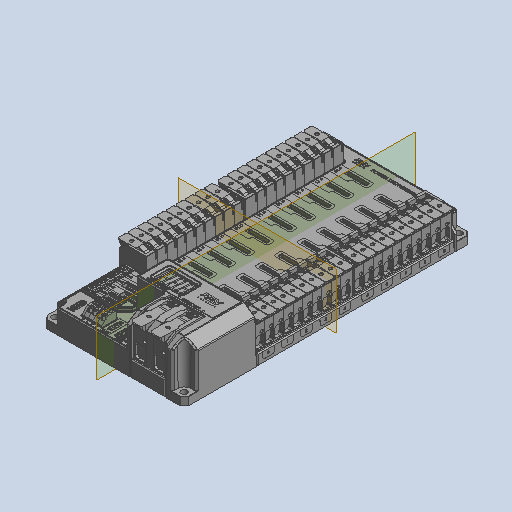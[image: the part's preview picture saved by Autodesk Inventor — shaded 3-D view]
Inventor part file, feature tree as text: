
AUTODESK INVENTOR PART (.ipt)
format: ipt  version: 2023 (Build 270158000, 158)  size: 30,594,048 bytes
history: native  units: mm (DEFAULTED — no unit token found)
features: other x402, plane x2
ambient origin geometry x8: Origin, YZ Plane, XZ Plane, XY Plane, X Axis, Y Axis, Z Axis, Center Point
bodies: Solid1 (feature_tree), Solid2 (feature_tree), Solid3 (feature_tree), Solid4 (feature_tree), Solid5 (feature_tree), Solid6 (feature_tree), Solid7 (feature_tree), Solid8 (feature_tree), Solid9 (feature_tree), Solid10 (feature_tree), Solid11 (feature_tree), Solid12 (feature_tree), Solid13 (feature_tree), Solid14 (feature_tree), Solid15 (feature_tree), Solid16 (feature_tree), Solid17 (feature_tree), Solid18 (feature_tree), Solid19 (feature_tree), Solid20 (feature_tree), Solid21 (feature_tree), Solid22 (feature_tree), Solid23 (feature_tree), Solid24 (feature_tree), Solid25 (feature_tree), Solid26 (feature_tree), Solid27 (feature_tree), Solid28 (feature_tree), Solid29 (feature_tree), Solid30 (feature_tree), Solid31 (feature_tree), Solid32 (feature_tree), Solid33 (feature_tree), Solid34 (feature_tree), Solid35 (feature_tree), Solid36 (feature_tree), Solid37 (feature_tree), Solid38 (feature_tree), Solid39 (feature_tree), Solid40 (feature_tree), Solid41 (feature_tree), Solid42 (feature_tree), Solid43 (feature_tree), Solid44 (feature_tree), Solid45 (feature_tree), Solid46 (feature_tree), Solid47 (feature_tree), Solid48 (feature_tree), Solid49 (feature_tree), Solid50 (feature_tree), Solid51 (feature_tree), Solid52 (feature_tree), Solid53 (feature_tree), Solid54 (feature_tree), Solid55 (feature_tree), Solid56 (feature_tree), Solid57 (feature_tree), Solid58 (feature_tree), Solid59 (feature_tree), Solid60 (feature_tree), Solid61 (feature_tree), Solid62 (feature_tree), Solid63 (feature_tree), Solid64 (feature_tree), Solid65 (feature_tree), Solid66 (feature_tree), Solid67 (feature_tree), Solid68 (feature_tree), Solid69 (feature_tree), Solid70 (feature_tree), Solid71 (feature_tree), Solid72 (feature_tree), Solid73 (feature_tree), Solid74 (feature_tree), Solid75 (feature_tree), Solid76 (feature_tree), Solid77 (feature_tree), Solid78 (feature_tree), Solid79 (feature_tree), Solid80 (feature_tree), Solid81 (feature_tree), Solid82 (feature_tree), Solid83 (feature_tree), Solid84 (feature_tree), Solid85 (feature_tree), Solid86 (feature_tree), Solid87 (feature_tree), Solid88 (feature_tree), Solid89 (feature_tree), Solid90 (feature_tree), Solid91 (feature_tree), Solid92 (feature_tree), Solid93 (feature_tree), Solid94 (feature_tree), Solid95 (feature_tree), Solid96 (feature_tree), Solid97 (feature_tree), Solid98 (feature_tree), Solid99 (feature_tree), Solid100 (feature_tree), Solid101 (feature_tree), Solid102 (feature_tree), Solid103 (feature_tree), Solid104 (feature_tree), Solid105 (feature_tree), Solid106 (feature_tree), Solid107 (feature_tree), Solid108 (feature_tree), Solid109 (feature_tree), Solid110 (feature_tree), Solid111 (feature_tree), Solid112 (feature_tree), Solid113 (feature_tree), Solid114 (feature_tree), Solid115 (feature_tree), Solid116 (feature_tree), Solid117 (feature_tree), Solid118 (feature_tree), Solid119 (feature_tree), Solid120 (feature_tree), Solid121 (feature_tree), Solid122 (feature_tree), Solid123 (feature_tree), Solid124 (feature_tree), Solid125 (feature_tree), Solid126 (feature_tree), Solid127 (feature_tree), Solid128 (feature_tree), Solid129 (feature_tree), Solid130 (feature_tree), Solid131 (feature_tree), Solid132 (feature_tree), Solid133 (feature_tree), Solid134 (feature_tree), Solid135 (feature_tree), Solid136 (feature_tree), Solid137 (feature_tree), Solid138 (feature_tree), Solid139 (feature_tree), Solid140 (feature_tree), Solid141 (feature_tree), Solid142 (feature_tree), Solid143 (feature_tree), Solid144 (feature_tree), Solid145 (feature_tree), Solid146 (feature_tree), Solid147 (feature_tree), Solid148 (feature_tree), Solid149 (feature_tree), Solid150 (feature_tree), Solid151 (feature_tree), Solid152 (feature_tree), Solid153 (feature_tree), Solid154 (feature_tree), Solid155 (feature_tree), Solid156 (feature_tree), Solid157 (feature_tree), Solid158 (feature_tree), Solid159 (feature_tree), Solid160 (feature_tree), Solid161 (feature_tree), Solid162 (feature_tree), Solid163 (feature_tree), Solid164 (feature_tree), Solid165 (feature_tree), Solid166 (feature_tree), Solid167 (feature_tree), Solid168 (feature_tree), Solid169 (feature_tree), Solid170 (feature_tree), Solid171 (feature_tree), Solid172 (feature_tree), Solid173 (feature_tree), Solid174 (feature_tree), Solid175 (feature_tree), Solid176 (feature_tree), Solid177 (feature_tree), Solid178 (feature_tree), Solid179 (feature_tree), Solid180 (feature_tree), Solid181 (feature_tree), Solid182 (feature_tree), Solid183 (feature_tree), Solid184 (feature_tree), Solid185 (feature_tree), Solid186 (feature_tree), Solid187 (feature_tree), Solid188 (feature_tree), Solid189 (feature_tree), Solid190 (feature_tree), Solid191 (feature_tree), Solid192 (feature_tree), Solid193 (feature_tree), Solid194 (feature_tree), Solid195 (feature_tree), Solid196 (feature_tree), Solid197 (feature_tree), Solid198 (feature_tree), Solid199 (feature_tree), Solid200 (feature_tree), Solid201 (feature_tree), Solid202 (feature_tree), Solid203 (feature_tree), Solid204 (feature_tree), Solid205 (feature_tree), Solid206 (feature_tree), Solid207 (feature_tree), Solid208 (feature_tree), Solid209 (feature_tree), Solid210 (feature_tree), Solid211 (feature_tree), Solid212 (feature_tree), Solid213 (feature_tree), Solid214 (feature_tree), Solid215 (feature_tree), Solid216 (feature_tree), Solid217 (feature_tree), Solid218 (feature_tree), Solid219 (feature_tree), Solid220 (feature_tree), Solid221 (feature_tree), Solid222 (feature_tree), Solid223 (feature_tree), Solid224 (feature_tree), Solid225 (feature_tree), Solid226 (feature_tree), Solid227 (feature_tree), Solid228 (feature_tree), Solid229 (feature_tree), Solid230 (feature_tree), Solid231 (feature_tree), Solid232 (feature_tree), Solid233 (feature_tree), Solid234 (feature_tree), Solid235 (feature_tree), Solid236 (feature_tree), Solid237 (feature_tree), Solid238 (feature_tree), Solid239 (feature_tree), Solid240 (feature_tree), Solid241 (feature_tree), Solid242 (feature_tree), Solid243 (feature_tree), Solid244 (feature_tree), Solid245 (feature_tree), Solid246 (feature_tree), Solid247 (feature_tree), Solid248 (feature_tree), Solid249 (feature_tree), Solid250 (feature_tree), Solid251 (feature_tree), Solid252 (feature_tree), Solid253 (feature_tree), Solid254 (feature_tree), Solid255 (feature_tree), Solid256 (feature_tree), Solid257 (feature_tree), Solid258 (feature_tree), Solid259 (feature_tree), Solid260 (feature_tree), Solid261 (feature_tree), Solid262 (feature_tree), Solid263 (feature_tree), Solid264 (feature_tree), Solid265 (feature_tree), Solid266 (feature_tree), Solid267 (feature_tree), Solid268 (feature_tree), Solid269 (feature_tree), Solid270 (feature_tree), Solid271 (feature_tree), Solid272 (feature_tree), Solid273 (feature_tree), Solid274 (feature_tree), Solid275 (feature_tree), Solid276 (feature_tree), Solid277 (feature_tree), Solid278 (feature_tree), Solid279 (feature_tree), Solid280 (feature_tree), Solid281 (feature_tree), Solid282 (feature_tree), Solid283 (feature_tree), Solid284 (feature_tree), Solid285 (feature_tree), Solid286 (feature_tree), Solid287 (feature_tree), Solid288 (feature_tree), Solid289 (feature_tree), Solid290 (feature_tree), Solid291 (feature_tree), Solid292 (feature_tree), Solid293 (feature_tree), Solid294 (feature_tree), Solid295 (feature_tree), Solid296 (feature_tree), Solid297 (feature_tree), Solid298 (feature_tree), Solid299 (feature_tree), Solid300 (feature_tree), Solid301 (feature_tree), Solid302 (feature_tree), Solid303 (feature_tree), Solid304 (feature_tree), Solid305 (feature_tree), Solid306 (feature_tree), Solid307 (feature_tree), Solid308 (feature_tree), Solid309 (feature_tree), Solid310 (feature_tree), Solid311 (feature_tree), Solid312 (feature_tree), Solid313 (feature_tree), Solid314 (feature_tree), Solid315 (feature_tree), Solid316 (feature_tree), Solid317 (feature_tree), Solid318 (feature_tree), Solid319 (feature_tree), Solid320 (feature_tree), Solid321 (feature_tree), Solid322 (feature_tree), Solid323 (feature_tree), Solid324 (feature_tree), Solid325 (feature_tree), Solid326 (feature_tree), Solid327 (feature_tree), Solid328 (feature_tree), Solid329 (feature_tree), Solid330 (feature_tree), Solid331 (feature_tree), Solid332 (feature_tree), Solid333 (feature_tree), Solid334 (feature_tree), Solid335 (feature_tree), Solid336 (feature_tree), Solid337 (feature_tree), Solid338 (feature_tree), Solid339 (feature_tree), Solid340 (feature_tree), Solid341 (feature_tree), Solid342 (feature_tree), Solid343 (feature_tree), Solid344 (feature_tree), Solid345 (feature_tree), Solid346 (feature_tree), Solid347 (feature_tree), Solid348 (feature_tree), Solid349 (feature_tree), Solid350 (feature_tree), Solid351 (feature_tree), Solid352 (feature_tree), Solid353 (feature_tree), Solid354 (feature_tree), Solid355 (feature_tree), Solid356 (feature_tree), Solid357 (feature_tree), Solid358 (feature_tree), Solid359 (feature_tree), Solid360 (feature_tree), Solid361 (feature_tree), Solid362 (feature_tree), Solid363 (feature_tree), Solid364 (feature_tree), Solid365 (feature_tree), Solid366 (feature_tree), Solid367 (feature_tree), Solid368 (feature_tree), Solid369 (feature_tree), Solid370 (feature_tree), Solid371 (feature_tree), Solid372 (feature_tree), Solid373 (feature_tree), Solid374 (feature_tree), Solid375 (feature_tree), Solid376 (feature_tree), Solid377 (feature_tree), Solid378 (feature_tree), Solid379 (feature_tree), Solid380 (feature_tree), Solid381 (feature_tree), Solid382 (feature_tree), Solid383 (feature_tree), Solid384 (feature_tree), Solid385 (feature_tree), Solid386 (feature_tree), Solid387 (feature_tree), Solid388 (feature_tree), Solid389 (feature_tree), Solid390 (feature_tree), Solid391 (feature_tree), Solid392 (feature_tree), Solid393 (feature_tree), Solid394 (feature_tree), Solid395 (feature_tree), Solid396 (feature_tree), Solid397 (feature_tree), Solid398 (feature_tree), Solid399 (feature_tree), Solid400 (feature_tree), Solid401 (feature_tree), Solid402 (feature_tree), Solid403 (feature_tree)
feature tree (404):
  plane  "Work Plane1"
  plane  "Work Plane2"
  other  "REV-11-1850-P01-1-solid1"
  other  "REV-11-1850-P02-1-solid1"
  other  "REV-11-1850-P02-1-solid2"
  other  "REV-11-1850-P02-1-solid3"
  other  "REV-11-1850-P02-1-solid4"
  other  "REV-11-1850-P02-1-solid5"
  other  "REV-11-1850-P02-1-solid6"
  other  "REV-11-1850-P02-1-solid7"
  other  "REV-11-1850-P02-1-solid8"
  other  "REV-11-1850-P02-1-solid9"
  other  "REV-11-1850-P02-1-solid10"
  other  "REV-11-1850-P02-1-solid11"
  other  "REV-11-1850-P02-1-solid12"
  other  "REV-11-1850-P02-1-solid13"
  other  "REV-11-1850-P02-1-solid14"
  other  "REV-11-1850-P02-1-solid15"
  other  "REV-11-1850-P02-1-solid16"
  other  "REV-11-1850-P02-1-solid17"
  other  "REV-11-1850-P02-1-solid18"
  other  "REV-11-1850-P02-1-solid19"
  other  "REV-11-1850-P02-1-solid20"
  other  "REV-11-1850-P02-1-solid21"
  other  "REV-11-1850-P02-1-solid22"
  other  "REV-11-1850-P02-1-solid23"
  other  "REV-11-1850-P02-1-solid24"
  other  "REV-11-1850-P02-1-solid25"
  other  "REV-11-1850-P02-1-solid26"
  other  "REV-11-1850-P02-1-solid27"
  other  "REV-11-1850-P02-1-solid28"
  other  "REV-11-1850-P02-1-solid29"
  other  "REV-11-1850-P02-1-solid30"
  other  "REV-11-1850-P02-1-solid31"
  other  "REV-11-1850-P02-1-solid32"
  other  "REV-11-1850-P02-1-solid33"
  other  "REV-11-1850-P03-1-solid1"
  other  "REV-11-1850-P03-1-solid2"
  other  "REV-11-1850-P03-1-solid3"
  other  "REV-11-1850-P03-1-solid4"
  other  "REV-11-1850-P03-1-solid5"
  other  "REV-11-1850-P03-1-solid6"
  other  "REV-11-1850-P03-1-solid7"
  other  "REV-11-1850-P03-1-solid8"
  other  "REV-11-1850-P03-1-solid9"
  other  "REV-11-1850-P03-1-solid10"
  other  "REV-11-1850-P03-1-solid11"
  other  "REV-11-1850-P03-1-solid12"
  other  "REV-11-1850-P03-1-solid13"
  other  "REV-11-1850-P03-1-solid14"
  other  "REV-11-1850-P03-1-solid15"
  other  "REV-11-1850-P03-1-solid16"
  other  "REV-11-1850-P03-1-solid17"
  other  "REV-11-1850-P03-1-solid18"
  other  "REV-11-1850-P03-1-solid19"
  other  "REV-11-1850-P03-1-solid20"
  other  "REV-11-1850-P03-1-solid21"
  other  "REV-11-1850-P03-1-solid22"
  other  "REV-11-1850-P03-1-solid23"
  other  "REV-11-1850-P03-1-solid24"
  other  "REV-11-1850-P03-1-solid25"
  other  "REV-11-1850-P03-1-solid26"
  other  "REV-11-1850-P03-1-solid27"
  other  "REV-11-1850-P03-1-solid28"
  other  "REV-11-1850-P03-1-solid29"
  other  "REV-11-1850-P03-1-solid30"
  other  "REV-11-1850-P03-1-solid31"
  other  "REV-11-1850-P03-1-solid32"
  other  "REV-11-1850-P03-1-solid33"
  other  "REV-11-1850-P03-1-solid34"
  other  "REV-11-1850-P03-1-solid35"
  other  "REV-11-1850-P03-1-solid36"
  other  "REV-11-1850-P03-1-solid37"
  other  "REV-11-1850-P03-1-solid38"
  other  "REV-11-1850-P03-1-solid39"
  other  "REV-11-1850-P03-1-solid40"
  other  "REV-11-1850-P04-1-solid1"
  other  "REV-11-1850-P04-1-solid2"
  other  "REV-11-1850-P04-1-solid3"
  other  "REV-11-1850-P04-1-solid4"
  other  "REV-11-1850-P04-1-solid5"
  other  "REV-11-1850-P04-1-solid6"
  other  "REV-11-1850-P04-1-solid7"
  other  "REV-11-1850-P04-1-solid8"
  other  "REV-11-1850-P04-1-solid9"
  other  "REV-11-1850-P04-1-solid10"
  other  "REV-11-1850-P04-1-solid11"
  other  "REV-11-1850-P04-1-solid12"
  other  "REV-11-1850-P04-1-solid13"
  other  "REV-11-1850-P04-1-solid14"
  other  "REV-11-1850-P04-1-solid15"
  other  "REV-11-1850-P04-1-solid16"
  other  "REV-11-1850-P04-1-solid17"
  other  "REV-11-1850-P04-1-solid18"
  other  "REV-11-1850-P04-1-solid19"
  other  "REV-11-1850-P04-1-solid20"
  other  "REV-11-1850-P04-1-solid21"
  other  "REV-11-1850-P04-1-solid22"
  other  "REV-11-1850-P04-1-solid23"
  other  "REV-11-1850-P04-1-solid24"
  other  "REV-11-1850-P04-1-solid25"
  other  "REV-11-1850-P04-1-solid26"
  other  "REV-11-1850-P04-1-solid27"
  other  "REV-11-1850-P04-1-solid28"
  other  "REV-11-1850-P04-1-solid29"
  other  "REV-11-1850-P04-1-solid30"
  other  "REV-11-1850-P04-1-solid31"
  other  "REV-11-1850-P04-1-solid32"
  other  "REV-11-1850-P04-1-solid33"
  other  "REV-11-1850-P04-1-solid34"
  other  "REV-11-1850-P04-1-solid35"
  other  "REV-11-1850-P04-1-solid36"
  other  "REV-11-1850-P04-1-solid37"
  other  "REV-11-1850-P04-1-solid38"
  other  "REV-11-1850-P04-1-solid39"
  other  "REV-11-1850-P04-1-solid40"
  other  "REV-11-1850-P04-1-solid41"
  other  "REV-11-1850-P04-1-solid42"
  other  "REV-11-1850-P04-1-solid43"
  other  "REV-11-1850-P04-1-solid44"
  other  "REV-11-1850-P04-1-solid45"
  other  "REV-11-1850-P04-1-solid46"
  other  "REV-11-1850-P04-1-solid47"
  other  "REV-11-1850-P04-1-solid48"
  other  "REV-11-1850-P04-1-solid49"
  other  "REV-11-1850-P04-1-solid50"
  other  "REV-11-1850-P04-1-solid51"
  other  "REV-11-1850-P04-1-solid52"
  other  "REV-11-1850-P04-1-solid53"
  other  "REV-11-1850-P04-1-solid54"
  other  "REV-11-1850-P04-1-solid55"
  other  "REV-11-1850-P04-1-solid56"
  other  "REV-11-1850-P04-1-solid57"
  other  "REV-11-1850-P04-1-solid58"
  other  "REV-11-1850-P04-1-solid59"
  other  "REV-11-1850-P04-1-solid60"
  other  "REV-11-1850-P04-1-solid61"
  other  "REV-11-1850-P04-1-solid62"
  other  "REV-11-1850-P04-1-solid63"
  other  "REV-11-1850-P04-1-solid64"
  other  "REV-11-1850-P04-1-solid65"
  other  "REV-11-1850-P04-1-solid66"
  other  "REV-11-1850-P04-1-solid67"
  other  "REV-11-1850-P04-1-solid68"
  other  "REV-11-1850-P04-1-solid69"
  other  "REV-11-1850-P04-1-solid70"
  other  "REV-11-1850-P04-1-solid71"
  other  "REV-11-1850-P04-1-solid72"
  other  "REV-11-1850-P04-1-solid73"
  other  "REV-11-1850-P04-1-solid74"
  other  "REV-11-1850-P04-1-solid75"
  other  "REV-11-1850-P04-1-solid76"
  other  "REV-11-1850-P04-1-solid77"
  other  "REV-11-1850-P04-1-solid78"
  other  "REV-11-1850-P04-1-solid79"
  other  "REV-11-1850-P04-1-solid80"
  other  "REV-11-1850-P04-1-solid81"
  other  "REV-11-1850-P04-1-solid82"
  other  "REV-11-1850-P04-1-solid83"
  other  "REV-11-1850-P04-1-solid84"
  other  "REV-11-1850-P04-1-solid85"
  other  "REV-11-1850-P04-1-solid86"
  other  "REV-11-1850-P04-1-solid87"
  other  "REV-11-1850-P04-1-solid88"
  other  "REV-11-1850-P04-1-solid89"
  other  "REV-11-1850-P04-1-solid90"
  other  "REV-11-1850-P04-1-solid91"
  other  "REV-11-1850-P04-1-solid92"
  other  "REV-11-1850-P04-1-solid93"
  other  "REV-11-1850-P04-1-solid94"
  other  "REV-11-1850-P04-1-solid95"
  other  "REV-11-1850-P04-1-solid96"
  other  "REV-11-1850-P04-1-solid97"
  other  "REV-11-1850-P04-1-solid98"
  other  "REV-11-1850-P04-1-solid99"
  other  "REV-11-1850-P04-1-solid100"
  other  "REV-11-1850-P04-1-solid101"
  other  "REV-11-1850-P04-1-solid102"
  other  "REV-11-1850-P04-1-solid103"
  other  "REV-11-1850-P04-1-solid104"
  other  "REV-11-1850-P04-1-solid105"
  other  "REV-11-1850-P04-1-solid106"
  other  "REV-11-1850-P04-1-solid107"
  other  "REV-11-1850-P05-1-solid1"
  other  "REV-11-1850-P05-1-solid2"
  other  "REV-11-1850-P05-1-solid3"
  other  "REV-11-1850-P05-1-solid4"
  other  "REV-11-1850-P05-1-solid5"
  other  "REV-11-1850-P05-1-solid6"
  other  "REV-11-1850-P05-1-solid7"
  other  "REV-11-1850-P05-1-solid8"
  other  "REV-11-1850-P05-1-solid9"
  other  "REV-11-1850-P05-1-solid10"
  other  "REV-11-1850-P05-1-solid11"
  other  "REV-11-1850-P05-1-solid12"
  other  "REV-11-1850-P05-1-solid13"
  other  "REV-11-1850-P05-1-solid14"
  other  "REV-11-1850-P05-1-solid15"
  other  "REV-11-1850-P05-1-solid16"
  other  "REV-11-1850-P05-1-solid17"
  other  "REV-11-1850-P05-1-solid18"
  other  "REV-11-1850-P05-1-solid19"
  other  "REV-11-1850-P05-1-solid20"
  other  "REV-11-1850-P05-1-solid21"
  other  "REV-11-1850-P05-1-solid22"
  other  "REV-11-1850-P05-1-solid23"
  other  "REV-11-1850-P05-1-solid24"
  other  "REV-11-1850-P05-1-solid25"
  other  "REV-11-1850-P05-1-solid26"
  other  "REV-11-1850-P05-1-solid27"
  other  "REV-11-1850-P05-1-solid28"
  other  "REV-11-1850-P05-1-solid29"
  other  "REV-11-1850-P05-1-solid30"
  other  "REV-11-1850-P05-1-solid31"
  other  "REV-11-1850-P05-1-solid32"
  other  "REV-11-1850-P05-1-solid33"
  other  "REV-11-1850-P05-1-solid34"
  other  "REV-11-1850-P05-1-solid35"
  other  "REV-11-1850-P05-1-solid36"
  other  "REV-11-1850-P06-1-solid1"
  other  "VOLTMETER DISPLAY-1-solid1"
  other  "VOLTMETER DISPLAY-1-solid2"
  other  "VOLTMETER DISPLAY-1-solid3"
  other  "M2X6 THREAD FORMING SCREW-1-solid1"
  other  "M2X6 THREAD FORMING SCREW-1-solid2"
  other  "M2X6 THREAD FORMING SCREW-3-solid1"
  other  "M2X6 THREAD FORMING SCREW-3-solid2"
  other  "M2X6 THREAD FORMING SCREW-4-solid1"
  other  "M2X6 THREAD FORMING SCREW-4-solid2"
  other  "M2X6 THREAD FORMING SCREW-5-solid1"
  other  "M2X6 THREAD FORMING SCREW-5-solid2"
  other  "M2X6 THREAD FORMING SCREW-6-solid1"
  other  "M2X6 THREAD FORMING SCREW-6-solid2"
  other  "M2X6 THREAD FORMING SCREW-7-solid1"
  other  "M2X6 THREAD FORMING SCREW-7-solid2"
  other  "M3X8 THREAD FORMING SCREW-1-solid1"
  other  "M3X8 THREAD FORMING SCREW-1-solid2"
  other  "M3X8 THREAD FORMING SCREW-2-solid1"
  other  "M3X8 THREAD FORMING SCREW-2-solid2"
  other  "M3X8 THREAD FORMING SCREW-3-solid1"
  other  "M3X8 THREAD FORMING SCREW-3-solid2"
  other  "M3X8 THREAD FORMING SCREW-4-solid1"
  other  "M3X8 THREAD FORMING SCREW-4-solid2"
  other  "REV-11-1850-F-CTL-1_REV-11-1850-F-CTL-1-solid1"
  other  "REV-11-1850-F-CTL-1_WAGO CAN 4-POLE BLOCK-01"
  other  "REV-11-1850-F-CTL-1_WAGO CAN 4-POLE BLOCK-02"
  other  "REV-11-1850-F-CTL-1_WAGO CAN 4-POLE BLOCK-03"
  other  "REV-11-1850-F-CTL-1_WAGO CAN 4-POLE BLOCK-04"
  other  "REV-11-1850-F-CTL-1_WAGO CAN 4-POLE BLOCK-05"
  other  "REV-11-1850-F-CTL-1_SWITCH-1-solid1"
  parser-record x1  (decoder bookkeeping rows leaked as tree rows — omitted from the tree; the rows remain in map.json)
  other  "NONE:1"
  other  "REV-11-1850-F-CTL-1_Low Profile Tack Switch-1-solid1"
  other  "REV-11-1850-F-CTL-1_LED-01"
  other  "REV-11-1850-F-PWR-1_REV-11-1850-F-PWR-1-solid1"
  other  "REV-11-1850-F-PWR-1_WAGO-01"
  other  "REV-11-1850-F-PWR-1_WAGO-02"
  other  "REV-11-1850-F-PWR-1_WAGO-03"
  other  "REV-11-1850-F-PWR-1_WAGO-04"
  other  "REV-11-1850-F-PWR-1_WAGO-05"
  other  "REV-11-1850-F-PWR-1_WAGO-06"
  other  "REV-11-1850-F-PWR-1_WAGO-07"
  other  "REV-11-1850-F-PWR-1_WAGO-08"
  other  "REV-11-1850-F-PWR-1_WAGO-09"
  other  "REV-11-1850-F-PWR-1_WAGO-10"
  other  "REV-11-1850-F-PWR-1_WAGO-11"
  other  "REV-11-1850-F-PWR-1_WAGO-12"
  other  "REV-11-1850-F-PWR-1_WAGO-13"
  other  "REV-11-1850-F-PWR-1_WAGO-14"
  other  "REV-11-1850-F-PWR-1_WAGO-15"
  other  "REV-11-1850-F-PWR-1_WAGO-16"
  other  "REV-11-1850-F-PWR-1_WAGO-17"
  other  "REV-11-1850-F-PWR-1_WAGO-18"
  other  "REV-11-1850-F-PWR-1_WAGO-19"
  other  "REV-11-1850-F-PWR-1_WAGO-20"
  other  "REV-11-1850-F-PWR-1_WAGO-21"
  other  "REV-11-1850-F-PWR-1_WAGO-22"
  other  "REV-11-1850-F-PWR-1_WAGO-23"
  other  "REV-11-1850-F-PWR-1_WAGO-24"
  other  "REV-11-1850-F-PWR-1_WAGO-25"
  other  "REV-11-1850-F-PWR-1_WAGO-26"
  other  "REV-11-1850-F-PWR-1_WAGO-27"
  other  "REV-11-1850-F-PWR-1_WAGO-28"
  other  "REV-11-1850-F-PWR-1_WAGO-29"
  other  "REV-11-1850-F-PWR-1_WAGO-30"
  other  "REV-11-1850-F-PWR-1_WAGO-31"
  other  "REV-11-1850-F-PWR-1_WAGO-32"
  other  "REV-11-1850-F-PWR-1_WAGO-33"
  other  "REV-11-1850-F-PWR-1_WAGO-34"
  other  "REV-11-1850-F-PWR-1_WAGO-35"
  other  "REV-11-1850-F-PWR-1_WAGO-36"
  other  "REV-11-1850-F-PWR-1_WAGO-37"
  other  "REV-11-1850-F-PWR-1_WAGO-38"
  other  "REV-11-1850-F-PWR-1_WAGO-39"
  other  "REV-11-1850-F-PWR-1_WAGO-40"
  other  "REV-11-1850-F-PWR-1_2 POLE WAGO INPUT-01"
  other  "REV-11-1850-F-PWR-1_2 POLE WAGO INPUT-02"
  other  "REV-11-1850-F-PWR-1_2 POLE WAGO INPUT-03"
  other  "REV-11-1850-F-PWR-1_2 POLE WAGO INPUT-04"
  other  "REV-11-1850-F-PWR-1_8 POLE WAGO POWER BLOCK OUTPUT-1_SPACER BLACK-1-solid1"
  other  "REV-11-1850-F-PWR-1_8 POLE WAGO POWER BLOCK OUTPUT-1_BLACK POLE-5-solid1"
  other  "REV-11-1850-F-PWR-1_8 POLE WAGO POWER BLOCK OUTPUT-1_RED POLE-5-solid1"
  other  "REV-11-1850-F-PWR-1_8 POLE WAGO POWER BLOCK OUTPUT-1_RED POLE-6-solid1"
  other  "REV-11-1850-F-PWR-1_8 POLE WAGO POWER BLOCK OUTPUT-1_RED POLE-7-solid1"
  other  "REV-11-1850-F-PWR-1_8 POLE WAGO POWER BLOCK OUTPUT-1_RED POLE-8-solid1"
  other  "REV-11-1850-F-PWR-1_8 POLE WAGO POWER BLOCK OUTPUT-1_BLACK POLE-7-solid1"
  other  "REV-11-1850-F-PWR-1_8 POLE WAGO POWER BLOCK OUTPUT-1_BLACK POLE-8-solid1"
  other  "REV-11-1850-F-PWR-1_8 POLE WAGO POWER BLOCK OUTPUT-1_BLACK POLE-9-solid1"
  other  "NONE:2"
  other  "REV-11-1850-F-PWR-1_SBH-02"
  other  "REV-11-1850-F-PWR-1_SBH-04"
  other  "NONE:3"
  other  "REV-11-1850-F-PWR-1_SBH-06"
  other  "REV-11-1850-F-PWR-1_SBH-07"
  other  "NONE:4"
  other  "REV-11-1850-F-PWR-1_SBH-09"
  other  "REV-11-1850-F-PWR-1_SBH-10"
  other  "NONE:5"
  other  "REV-11-1850-F-PWR-1_SBH-12"
  other  "REV-11-1850-F-PWR-1_SBH-13"
  other  "NONE:6"
  other  "REV-11-1850-F-PWR-1_LBH-02"
  other  "REV-11-1850-F-PWR-1_LBH-03"
  other  "NONE:7"
  other  "REV-11-1850-F-PWR-1_LBH-05"
  other  "REV-11-1850-F-PWR-1_LBH-06"
  other  "REV-11-1850-F-PWR-1_0606 LED-1-solid1"
  other  "REV-11-1850-F-PWR-1_0606 LED-2-solid1"
  other  "REV-11-1850-F-PWR-1_0606 LED-3-solid1"
  other  "REV-11-1850-F-PWR-1_0606 LED-4-solid1"
  other  "REV-11-1850-F-PWR-1_0606 LED-5-solid1"
  other  "REV-11-1850-F-PWR-1_0606 LED-6-solid1"
  other  "REV-11-1850-F-PWR-1_0606 LED-7-solid1"
  other  "REV-11-1850-F-PWR-1_0606 LED-8-solid1"
  other  "REV-11-1850-F-PWR-1_0606 LED-9-solid1"
  other  "REV-11-1850-F-PWR-1_0606 LED-10-solid1"
  other  "NONE:8"
  other  "REV-11-1850-F-PWR-1_LBH-08"
  other  "REV-11-1850-F-PWR-1_LBH-09"
  other  "NONE:9"
  other  "REV-11-1850-F-PWR-1_LBH-11"
  other  "REV-11-1850-F-PWR-1_LBH-12"
  other  "NONE:10"
  other  "REV-11-1850-F-PWR-1_LBH-14"
  other  "REV-11-1850-F-PWR-1_LBH-15"
  other  "NONE:11"
  other  "REV-11-1850-F-PWR-1_LBH-17"
  other  "REV-11-1850-F-PWR-1_LBH-18"
  other  "NONE:12"
  other  "REV-11-1850-F-PWR-1_LBH-20"
  other  "REV-11-1850-F-PWR-1_LBH-21"
  other  "NONE:13"
  other  "REV-11-1850-F-PWR-1_LBH-23"
  other  "REV-11-1850-F-PWR-1_LBH-24"
  other  "NONE:14"
  other  "REV-11-1850-F-PWR-1_LBH-26"
  other  "REV-11-1850-F-PWR-1_LBH-27"
  other  "NONE:15"
  other  "REV-11-1850-F-PWR-1_LBH-29"
  other  "REV-11-1850-F-PWR-1_LBH-30"
  other  "REV-11-1850-F-PWR-1_0606 LED-11-solid1"
  other  "REV-11-1850-F-PWR-1_0606 LED-12-solid1"
  other  "NONE:16"
  other  "REV-11-1850-F-PWR-1_LBH-32"
  other  "REV-11-1850-F-PWR-1_LBH-33"
  other  "NONE:17"
  other  "REV-11-1850-F-PWR-1_LBH-35"
  other  "REV-11-1850-F-PWR-1_LBH-36"
  other  "REV-11-1850-F-PWR-1_0606 LED-13-solid1"
  other  "REV-11-1850-F-PWR-1_0606 LED-14-solid1"
  other  "REV-11-1850-F-PWR-1_0606 LED-15-solid1"
  other  "REV-11-1850-F-PWR-1_0606 LED-16-solid1"
  other  "REV-11-1850-F-PWR-1_0606 LED-17-solid1"
  other  "REV-11-1850-F-PWR-1_0606 LED-18-solid1"
  other  "REV-11-1850-F-PWR-1_0606 LED-19-solid1"
  other  "REV-11-1850-F-PWR-1_0606 LED-20-solid1"
  other  "NONE:18"
  other  "REV-11-1850-F-PWR-1_LBH-38"
  other  "REV-11-1850-F-PWR-1_LBH-39"
  other  "NONE:19"
  other  "REV-11-1850-F-PWR-1_LBH-41"
  other  "REV-11-1850-F-PWR-1_LBH-42"
  other  "NONE:20"
  other  "REV-11-1850-F-PWR-1_LBH-44"
  other  "REV-11-1850-F-PWR-1_LBH-45"
  other  "NONE:21"
  other  "REV-11-1850-F-PWR-1_LBH-47"
  other  "REV-11-1850-F-PWR-1_LBH-48"
  other  "NONE:22"
  other  "REV-11-1850-F-PWR-1_LBH-50"
  other  "REV-11-1850-F-PWR-1_LBH-51"
  other  "NONE:23"
  other  "REV-11-1850-F-PWR-1_LBH-53"
  other  "REV-11-1850-F-PWR-1_LBH-54"
  other  "NONE:24"
  other  "REV-11-1850-F-PWR-1_LBH-56"
  other  "REV-11-1850-F-PWR-1_LBH-57"
  other  "NONE:25"
  other  "REV-11-1850-F-PWR-1_LBH-59"
  other  "REV-11-1850-F-PWR-1_LBH-60"
  other  "REV-11-1850-F-PWR-1_0606 LED-21-solid1"
  other  "REV-11-1850-F-PWR-1_0606 LED-22-solid1"
  other  "REV-11-1850-F-PWR-1_0606 LED-23-solid1"
  other  "REV-11-1850-F-PWR-1_0606 LED-24-solid1"
